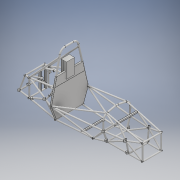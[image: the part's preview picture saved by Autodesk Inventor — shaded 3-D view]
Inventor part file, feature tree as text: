
AUTODESK INVENTOR PART (.ipt)
format: ipt  version: 2018 (Build 220112000, 112)  size: 2,467,840 bytes
history: native  units: mm
features: other x22, extrude x2, sketch x2, fillet x1, projected_geometry x1
ambient origin geometry x8: Origin, YZ Plane, XZ Plane, XY Plane, X Axis, Y Axis, Z Axis, Center Point
bodies: Body1 (feature_tree), Body2 (feature_tree), Body3 (feature_tree), Body4 (feature_tree), Body5 (feature_tree), Body6 (feature_tree), Body7 (feature_tree), Body8 (feature_tree), Body9 (feature_tree), Body10 (feature_tree), Body11 (feature_tree)
feature tree (28):
  other  "ソリッド1"
  extrude  "押し出し1"  Depth=100.0mm TaperAngle=0.0deg
  extrude  "押し出し4"  Depth=150.0mm
  fillet  "フィレット1"  Radius=28.5mm
  other  "ソリッド2"
  other  "ソリッド3"
  other  "ソリッド4"
  other  "ソリッド5"
  other  "ソリッド6"
  other  "ソリッド7"
  other  "ソリッド8"
  other  "ソリッド9"
  other  "ソリッド10"
  other  "ソリッド16"
  sketch  "スケッチ1"
  projected_geometry  "投影ループ1"
  sketch  "スケッチ5"
  other  "Brep With Voids"
  other  "suspension support.1"
  other  "suspension support.2"
  other  "seat stay lower.1"
  other  "seat stay lower.2"
  other  "seat stay lower.3"
  other  "main hoop brace support upper 2.1"
  other  "main hoop brace support upper 2.2"
  other  "suspension support 2.1"
  other  "suspension support 2.2"
  other  "headrest support"
